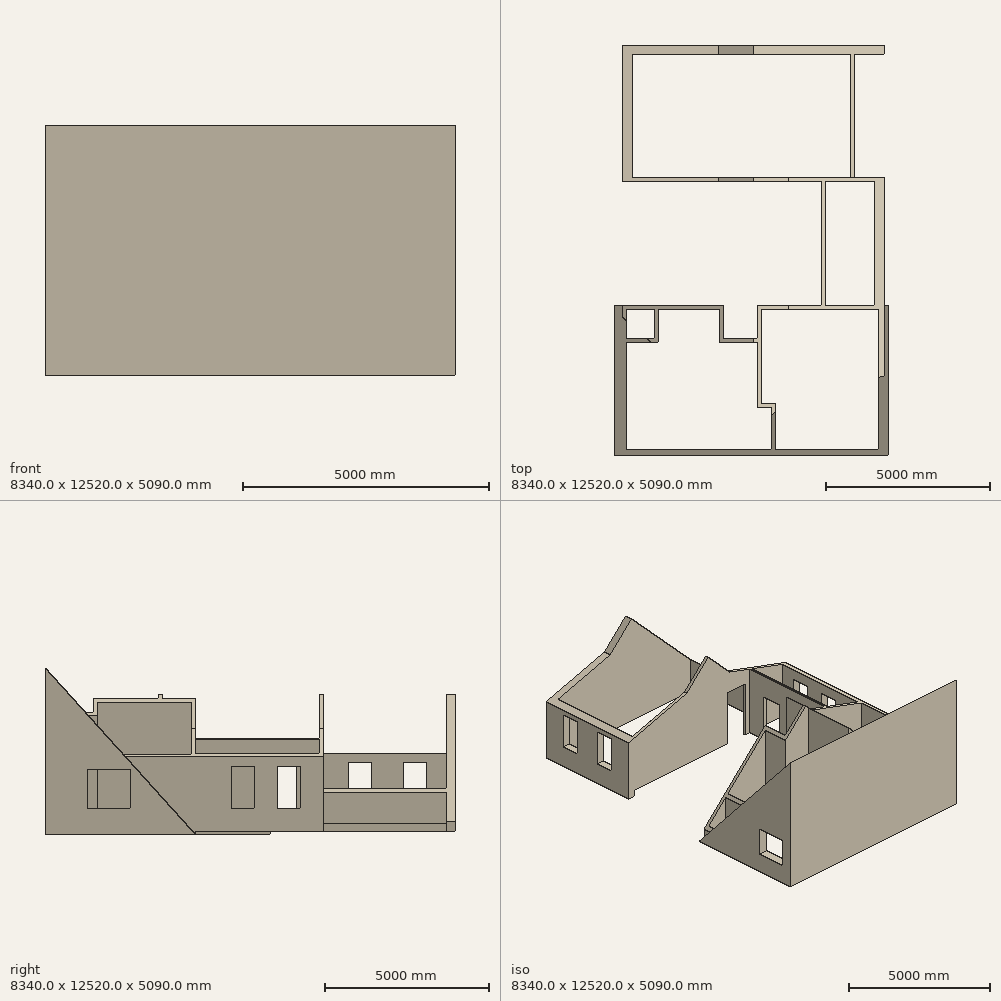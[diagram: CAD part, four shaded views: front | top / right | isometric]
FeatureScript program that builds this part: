
annotation { "Feature Type Name" : "Feature", "Feature Type Description" : "" }
export const myFeature = defineFeature(function(context is Context, id is Id, definition is map)
    precondition{}
    {
        {
            var Q0;
            Q0=qCreatedBy(makeId("Right.planeOp"),FACE);
            var sketch = newSketch(context, id + "F0", { "sketchPlane" : qUnion([Q0])});
            skLineSegment(sketch, "E0", {"start": v(2296.26, -2868.99) * mm, "end": v(-2293.74, -2868.99) * mm});
            skLineSegment(sketch, "E1", {"start": v(-2293.74, -2868.99) * mm, "end": v(-2293.74, 2221.01) * mm});
            skLineSegment(sketch, "E2", {"start": v(-2293.74, 2221.01) * mm, "end": v(2296.26, -2868.99) * mm});
            skSolve(sketch);
        }
        {
            var Q0;
            Q0=makeQuery(id+"F0.imprint","IMPRINT",FACE,{"disambiguationData":[TD([[makeQuery(id+"F0.imprint","IMPRINT",EDGE,{"derivedFrom":sQuery(id+"F0.wireOp",EDGE,"E0")}),-1.0]])]});
            extrude(context, id + "F1", {"entities" : qUnion([Q0]), "depth" : 8340 * mm});
        }
        {
            var Q0;
            Q0=makeQuery(id+"F1.opExtrude","SWEPT_FACE",FACE,{"disambiguationData":[OSD([sQuery(id+"F0.wireOp",EDGE,"E1")])]});
            cPlane(context, id + "F2", {"entities" : qUnion([Q0]), "cplaneType" : CPlaneType.OFFSET, "offset" : 12520 * mm, "oppositeDirection" : true, "width" : 150 * mm, "height" : 150 * mm});
        }
        {
            var Q0;
            Q0=qCreatedBy(id+"F2.planeOp",FACE);
            var sketch = newSketch(context, id + "F3", { "sketchPlane" : qUnion([Q0])});
            skPoint(sketch, "E3.0", {"position": v(8220, -2868.99) * mm});
            skPoint(sketch, "E4.0", {"position": v(0, -2868.99) * mm});
            skLineSegment(sketch, "E5", {"start": v(8220, -2868.99) * mm, "end": v(230, -2868.99) * mm});
            skLineSegment(sketch, "E6", {"start": v(8220, -2868.99) * mm, "end": v(8220, -2468.99) * mm});
            skLineSegment(sketch, "E7", {"start": v(8220, -2468.99) * mm, "end": v(4225, 1421.01) * mm});
            skLineSegment(sketch, "E8", {"start": v(230, -2868.99) * mm, "end": v(230, -2468.99) * mm});
            skLineSegment(sketch, "E9", {"start": v(230, -2468.99) * mm, "end": v(4225, 1421.01) * mm});
            skSolve(sketch);
        }
        {
            var Q0;
            Q0=makeQuery(id+"F3.imprint","IMPRINT",FACE,{"disambiguationData":[TD([[makeQuery(id+"F3.imprint","IMPRINT",EDGE,{"derivedFrom":sQuery(id+"F3.wireOp",EDGE,"E5")}),-1.0]])]});
            extrude(context, id + "F4", {"entities" : qUnion([Q0]), "operationType" : NewBodyOperationType.ADD, "endBound" : BoundingType.UP_TO_NEXT, "depth" : 25 * mm});
        }
        {
            var Q0;
            Q0=makeQuery(id+"F4.opExtrude","CAP_FACE",FACE,{"disambiguationData":[OSD([sQuery(id+"F3.wireOp",EDGE,"E5"),sQuery(id+"F3.wireOp",EDGE,"wZPg0SDw-hQ3W-XM3Z-Tp2p-s9tjZs1w4FBg"),sQuery(id+"F3.wireOp",EDGE,"RhiNAI7Q-V7pc-C4zH-MZjU-NtJVtZchHZu0")])],"isStart":true});
            var sketch = newSketch(context, id + "F5", { "sketchPlane" : qUnion([Q0])});
            skLineSegment(sketch, "E10", {"start": v(-230, -2868.99) * mm, "end": v(-230, -468.99) * mm});
            skLineSegment(sketch, "E11", {"start": v(-230, -468.99) * mm, "end": v(-3150.31, 374.57) * mm});
            skLineSegment(sketch, "E12", {"start": v(-3150.31, 374.57) * mm, "end": v(-230, -2868.99) * mm});
            skSolve(sketch);
        }
        {
            var Q0;
            Q0=makeQuery(id+"F5.imprint","IMPRINT",FACE,{"disambiguationData":[TD([[makeQuery(id+"F5.imprint","IMPRINT",EDGE,{"derivedFrom":sQuery(id+"F5.wireOp",EDGE,"E10")}),1.0]])]});
            extrude(context, id + "F6", {"entities" : qUnion([Q0]), "operationType" : NewBodyOperationType.ADD, "oppositeDirection" : true, "depth" : 4150 * mm});
        }
        {
            var Q0;
            Q0=makeQuery(id+"F1.opExtrude","SWEPT_FACE",FACE,{"disambiguationData":[OSD([sQuery(id+"F0.wireOp",EDGE,"E1")])]});
            cPlane(context, id + "F7", {"entities" : qUnion([Q0]), "cplaneType" : CPlaneType.OFFSET, "offset" : 8490 * mm, "oppositeDirection" : true, "width" : 150 * mm, "height" : 150 * mm});
        }
        {
            var Q0;
            Q0=qCreatedBy(id+"F7.planeOp",FACE);
            var sketch = newSketch(context, id + "F8", { "sketchPlane" : qUnion([Q0])});
            skPoint(sketch, "E13.0", {"position": v(8220, -2868.99) * mm});
            skLineSegment(sketch, "E14", {"start": v(8220, -2868.99) * mm, "end": v(8220, -468.99) * mm});
            skLineSegment(sketch, "E15", {"start": v(8220, -468.99) * mm, "end": v(5299.69, 374.57) * mm});
            skLineSegment(sketch, "E16", {"start": v(5299.69, 374.57) * mm, "end": v(8220, -2868.99) * mm});
            skPoint(sketch, "E17.0", {"position": v(3150.31, 374.57) * mm});
            skSolve(sketch);
        }
        {
            var Q0;
            {var subQ0=sQuery(id+"F8.wireOp",EDGE,"E14");Q0=makeQuery(id+"F8.imprint","IMPRINT",FACE,{"disambiguationData":[TD([[makeQuery(id+"F8.imprint","IMPRINT",EDGE,{"derivedFrom":subQ0}),1.0]])]});}
            extrude(context, id + "F9", {"entities" : qUnion([Q0]), "operationType" : NewBodyOperationType.ADD, "depth" : 8000 * mm});
        }
        {
            var Q0;
            Q0=makeQuery(id+"F4.boolean.opBoolean","MERGE",FACE,{"derivedFrom":[makeQuery(id+"F1.opExtrude","SWEPT_FACE",FACE,{"disambiguationData":[OSD([sQuery(id+"F0.wireOp",EDGE,"E0")])]}),makeQuery(id+"F4.opExtrude","SWEPT_FACE",FACE,{"disambiguationData":[OSD([sQuery(id+"F3.wireOp",EDGE,"E5")])]})]});
            cPlane(context, id + "F10", {"entities" : qUnion([Q0]), "cplaneType" : CPlaneType.OFFSET, "offset" : 6000 * mm, "oppositeDirection" : true, "width" : 150 * mm, "height" : 150 * mm});
        }
        {
            var Q0;
            Q0=qCreatedBy(id+"F10.planeOp",FACE);
            var sketch = newSketch(context, id + "F11", { "sketchPlane" : qUnion([Q0])});
            skLineSegment(sketch, "E18.0", {"start": v(230, -10226.26) * mm, "end": v(3150.31, -10226.26) * mm});
            skLineSegment(sketch, "E19.0", {"start": v(3150.31, -10226.26) * mm, "end": v(8220, -10226.26) * mm});
            skLineSegment(sketch, "E20", {"start": v(360, -1154.29) * mm, "end": v(360, 2113.74) * mm});
            skLineSegment(sketch, "E21", {"start": v(360, 2113.74) * mm, "end": v(4780, 2113.74) * mm});
            skLineSegment(sketch, "E22", {"start": v(4780, 2113.74) * mm, "end": v(4780, 833.74) * mm});
            skLineSegment(sketch, "E23", {"start": v(4780, 833.74) * mm, "end": v(4360, 833.74) * mm});
            skLineSegment(sketch, "E24", {"start": v(4360, 833.74) * mm, "end": v(4360, -1165.91) * mm});
            skLineSegment(sketch, "E25", {"start": v(4480, -2176.26) * mm, "end": v(4480, 713.74) * mm});
            skLineSegment(sketch, "E26", {"start": v(4480, 713.74) * mm, "end": v(4900, 713.74) * mm});
            skLineSegment(sketch, "E27", {"start": v(4900, 713.74) * mm, "end": v(4900, 2113.74) * mm});
            skLineSegment(sketch, "E28", {"start": v(4900, 2113.74) * mm, "end": v(8040, 2113.74) * mm});
            skLineSegment(sketch, "E29", {"start": v(8040, 2113.74) * mm, "end": v(8040, -2176.26) * mm});
            skLineSegment(sketch, "E30", {"start": v(8040, -2176.26) * mm, "end": v(4480, -2176.26) * mm});
            skLineSegment(sketch, "E31", {"start": v(530, -9936.26) * mm, "end": v(530, -6196.26) * mm});
            skLineSegment(sketch, "E32", {"start": v(7183.26, -6196.26) * mm, "end": v(7183.26, -9936.26) * mm});
            skLineSegment(sketch, "E33", {"start": v(7183.26, -9936.26) * mm, "end": v(530, -9936.26) * mm});
            skLineSegment(sketch, "E34", {"start": v(6430, -6076.26) * mm, "end": v(6430, -2296.26) * mm});
            skLineSegment(sketch, "E35", {"start": v(6430, -2296.26) * mm, "end": v(7930, -2296.26) * mm});
            skLineSegment(sketch, "E36", {"start": v(7930, -2296.26) * mm, "end": v(7930, -6076.26) * mm});
            skLineSegment(sketch, "E37", {"start": v(7930, -6076.26) * mm, "end": v(6430, -6076.26) * mm});
            skLineSegment(sketch, "E38", {"start": v(7183.26, -6196.26) * mm, "end": v(6310, -6196.26) * mm});
            skLineSegment(sketch, "E39", {"start": v(6310, -6196.26) * mm, "end": v(6310, -6196.26) * mm});
            skLineSegment(sketch, "E40", {"start": v(6310, -6196.26) * mm, "end": v(530, -6196.26) * mm});
            skLineSegment(sketch, "E41", {"start": v(6310, -2296.26) * mm, "end": v(6310, -6076.26) * mm});
            skLineSegment(sketch, "E42", {"start": v(-2.05, -2296.26) * mm, "end": v(-2.05, -6076.26) * mm});
            skLineSegment(sketch, "E43", {"start": v(360, -1154.29) * mm, "end": v(1319.1, -1154.29) * mm});
            skLineSegment(sketch, "E44", {"start": v(1319.1, -1154.29) * mm, "end": v(1319.1, -2176.26) * mm});
            skLineSegment(sketch, "E45", {"start": v(1199.1, -1274.29) * mm, "end": v(360, -1274.29) * mm});
            skLineSegment(sketch, "E46", {"start": v(360, -1274.29) * mm, "end": v(360, -2176.26) * mm});
            skLineSegment(sketch, "E47", {"start": v(360, -2176.26) * mm, "end": v(1199.1, -2176.26) * mm});
            skLineSegment(sketch, "E48", {"start": v(1199.1, -2176.26) * mm, "end": v(1199.1, -1274.29) * mm});
            skLineSegment(sketch, "E49", {"start": v(-2.05, -6076.26) * mm, "end": v(4755, -6076.26) * mm});
            skLineSegment(sketch, "E50", {"start": v(6310, -6076.26) * mm, "end": v(4755, -6076.26) * mm});
            skLineSegment(sketch, "E51", {"start": v(4755, -6076.26) * mm, "end": v(4755, -6076.26) * mm});
            skLineSegment(sketch, "E52.bottom", {"start": v(7303.26, -9936.26) * mm, "end": v(6644.3, -9936.26) * mm});
            skLineSegment(sketch, "E52.top", {"start": v(7303.26, -6196.26) * mm, "end": v(6878.23, -6196.26) * mm});
            skLineSegment(sketch, "E52.right", {"start": v(7303.26, -9936.26) * mm, "end": v(7303.26, -6196.26) * mm});
            skLineSegment(sketch, "E53", {"start": v(4360, -1165.91) * mm, "end": v(3200, -1165.91) * mm});
            skLineSegment(sketch, "E54", {"start": v(3200, -1165.91) * mm, "end": v(3200, -2176.26) * mm});
            skLineSegment(sketch, "E55", {"start": v(3200, -2176.26) * mm, "end": v(1319.1, -2176.26) * mm});
            skLineSegment(sketch, "E56", {"start": v(-2.05, -2296.26) * mm, "end": v(3320, -2296.26) * mm});
            skLineSegment(sketch, "E57", {"start": v(3320, -2296.26) * mm, "end": v(3320, -1285.91) * mm});
            skLineSegment(sketch, "E58", {"start": v(3320, -1285.91) * mm, "end": v(4360, -1285.91) * mm});
            skLineSegment(sketch, "E59", {"start": v(4360, -1285.91) * mm, "end": v(4360, -2296.26) * mm});
            skLineSegment(sketch, "E60", {"start": v(4360, -2296.26) * mm, "end": v(6310, -2296.26) * mm});
            skPoint(sketch, "E61.0", {"position": v(8220, -10226.26) * mm});
            skPoint(sketch, "E62.0", {"position": v(0, 2293.74) * mm});
            skPoint(sketch, "E63.0", {"position": v(8340, 2293.74) * mm});
            skLineSegment(sketch, "E64", {"start": v(-2.05, -2296.26) * mm, "end": v(0, 2293.74) * mm});
            skLineSegment(sketch, "E65", {"start": v(0, 2293.74) * mm, "end": v(8340, 2293.74) * mm});
            skLineSegment(sketch, "E66.bottom", {"start": v(7303.26, -9936.26) * mm, "end": v(8220, -9936.26) * mm});
            skLineSegment(sketch, "E66.left", {"start": v(7303.26, -9936.26) * mm, "end": v(7303.26, -7396.26) * mm});
            skLineSegment(sketch, "E66.right", {"start": v(8220, -9936.26) * mm, "end": v(8220, -6196.26) * mm});
            skLineSegment(sketch, "E67.0.0", {"start": v(5299.69, 628.68) * mm, "end": v(5299.69, 628.68) * mm});
            skLineSegment(sketch, "E67.0.1", {"start": v(8220, -2296.26) * mm, "end": v(8220, -6196.26) * mm});
            skLineSegment(sketch, "E68", {"start": v(7303.26, -6196.26) * mm, "end": v(8220, -6196.26) * mm});
            skPoint(sketch, "E69.0", {"position": v(8220, -2296.26) * mm});
            skLineSegment(sketch, "E70", {"start": v(8220, -2296.26) * mm, "end": v(8340, -2296.26) * mm});
            skPoint(sketch, "E71.0", {"position": v(8340, -2296.26) * mm});
            skLineSegment(sketch, "E72", {"start": v(8340, -2296.26) * mm, "end": v(8340, 2293.74) * mm});
            skSolve(sketch);
        }
        {
            var Q0;
            Q0=makeQuery(id+"F11.imprint","IMPRINT",FACE,{"disambiguationData":[TD([[makeQuery(id+"F11.imprint","IMPRINT",EDGE,{"derivedFrom":sQuery(id+"F11.wireOp",EDGE,"E25")}),-1.0]])]});
            var Q1;
            Q1=makeQuery(id+"F11.imprint","IMPRINT",FACE,{"disambiguationData":[TD([[makeQuery(id+"F11.imprint","IMPRINT",EDGE,{"derivedFrom":sQuery(id+"F11.wireOp",EDGE,"E41")}),-1.0]])]});
            var Q2;
            Q2=makeQuery(id+"F11.imprint","IMPRINT",FACE,{"disambiguationData":[TD([[makeQuery(id+"F11.imprint","IMPRINT",EDGE,{"derivedFrom":sQuery(id+"F11.wireOp",EDGE,"E34")}),-1.0]])]});
            var Q3;
            Q3=makeQuery(id+"F11.imprint","IMPRINT",FACE,{"disambiguationData":[TD([[makeQuery(id+"F11.imprint","IMPRINT",EDGE,{"derivedFrom":sQuery(id+"F11.wireOp",EDGE,"E31")}),-1.0]])]});
            var Q4;
            Q4=makeQuery(id+"F11.imprint","IMPRINT",FACE,{"disambiguationData":[TD([[makeQuery(id+"F11.imprint","IMPRINT",EDGE,{"derivedFrom":sQuery(id+"F11.wireOp",EDGE,"E20")}),-1.0]])]});
            var Q5;
            Q5=makeQuery(id+"F11.imprint","IMPRINT",FACE,{"disambiguationData":[TD([[makeQuery(id+"F11.imprint","IMPRINT",EDGE,{"derivedFrom":sQuery(id+"F11.wireOp",EDGE,"E45")}),1.0]])]});
            var Q6;
            Q6=makeQuery(id+"F11.imprint","IMPRINT",FACE,{"disambiguationData":[TD([[makeQuery(id+"F11.imprint","IMPRINT",EDGE,{"derivedFrom":sQuery(id+"F11.wireOp",EDGE,"E66.bottom")}),1.0]])]});
            extrude(context, id + "F12", {"entities" : qUnion([Q0, Q1, Q2, Q3, Q4, Q5, Q6]), "operationType" : NewBodyOperationType.REMOVE, "endBound" : BoundingType.THROUGH_ALL, "depth" : 25 * mm});
        }
        {
            var Q0;
            Q0=makeQuery(id+"F12.boolean.opBoolean","COPY",FACE,{"derivedFrom":makeQuery(id+"F12.opExtrude","SWEPT_FACE",FACE,{"disambiguationData":[OSD([sQuery(id+"F11.wireOp",EDGE,"E41")])]})});
            var sketch = newSketch(context, id + "F13", { "sketchPlane" : qUnion([Q0])});
            skLineSegment(sketch, "E73.bottom", {"start": v(-5376.26, -2868.99) * mm, "end": v(-4576.26, -2868.99) * mm});
            skLineSegment(sketch, "E73.top", {"start": v(-5376.26, -768.99) * mm, "end": v(-4576.26, -768.99) * mm});
            skLineSegment(sketch, "E73.left", {"start": v(-5376.26, -2868.99) * mm, "end": v(-5376.26, -768.99) * mm});
            skLineSegment(sketch, "E73.right", {"start": v(-4576.26, -2868.99) * mm, "end": v(-4576.26, -768.99) * mm});
            skSolve(sketch);
        }
        {
            var Q0;
            Q0=makeQuery(id+"F13.imprint","IMPRINT",FACE,{"disambiguationData":[TD([[makeQuery(id+"F13.imprint","IMPRINT",EDGE,{"derivedFrom":sQuery(id+"F13.wireOp",EDGE,"E73.bottom")}),1.0]])]});
            extrude(context, id + "F14", {"entities" : qUnion([Q0]), "operationType" : NewBodyOperationType.REMOVE, "endBound" : BoundingType.UP_TO_NEXT, "oppositeDirection" : true, "depth" : 25 * mm});
        }
        {
            var Q0;
            Q0=makeQuery(id+"F6.opExtrude","SWEPT_FACE",FACE,{"disambiguationData":[OSD([sQuery(id+"F5.wireOp",EDGE,"E10")])]});
            var sketch = newSketch(context, id + "F15", { "sketchPlane" : qUnion([Q0])});
            skLineSegment(sketch, "E74.bottom", {"start": v(-9351.26, -668.99) * mm, "end": v(-8651.26, -668.99) * mm});
            skLineSegment(sketch, "E74.top", {"start": v(-9351.26, -1968.99) * mm, "end": v(-8651.26, -1968.99) * mm});
            skLineSegment(sketch, "E74.left", {"start": v(-9351.26, -668.99) * mm, "end": v(-9351.26, -1968.99) * mm});
            skLineSegment(sketch, "E74.right", {"start": v(-8651.26, -668.99) * mm, "end": v(-8651.26, -1968.99) * mm});
            skLineSegment(sketch, "E75.bottom", {"start": v(-7651.26, -668.99) * mm, "end": v(-6951.26, -668.99) * mm});
            skLineSegment(sketch, "E75.top", {"start": v(-7651.26, -1968.99) * mm, "end": v(-6951.26, -1968.99) * mm});
            skLineSegment(sketch, "E75.left", {"start": v(-7651.26, -668.99) * mm, "end": v(-7651.26, -1968.99) * mm});
            skLineSegment(sketch, "E75.right", {"start": v(-6951.26, -668.99) * mm, "end": v(-6951.26, -1968.99) * mm});
            skSolve(sketch);
        }
        {
            var Q0;
            Q0=makeQuery(id+"F15.imprint","IMPRINT",FACE,{"disambiguationData":[TD([[makeQuery(id+"F15.imprint","IMPRINT",EDGE,{"derivedFrom":sQuery(id+"F15.wireOp",EDGE,"E74.bottom")}),-1.0]])]});
            var Q1;
            Q1=makeQuery(id+"F15.imprint","IMPRINT",FACE,{"disambiguationData":[TD([[makeQuery(id+"F15.imprint","IMPRINT",EDGE,{"derivedFrom":sQuery(id+"F15.wireOp",EDGE,"E75.bottom")}),-1.0]])]});
            extrude(context, id + "F16", {"entities" : qUnion([Q0, Q1]), "operationType" : NewBodyOperationType.REMOVE, "endBound" : BoundingType.UP_TO_NEXT, "oppositeDirection" : true, "depth" : 25 * mm});
        }
        {
            var Q0;
            Q0=makeQuery(id+"F1.opExtrude","CAP_FACE",FACE,{"disambiguationData":[OSD([sQuery(id+"F0.wireOp",EDGE,"E0"),sQuery(id+"F0.wireOp",EDGE,"E1"),sQuery(id+"F0.wireOp",EDGE,"E2")])],"isStart":true});
            var sketch = newSketch(context, id + "F17", { "sketchPlane" : qUnion([Q0])});
            skLineSegment(sketch, "E76.bottom", {"start": v(733.74, -1138.99) * mm, "end": v(1863.74, -1138.99) * mm});
            skLineSegment(sketch, "E76.top", {"start": v(733.74, -2168.99) * mm, "end": v(1863.74, -2168.99) * mm});
            skLineSegment(sketch, "E76.left", {"start": v(733.74, -1138.99) * mm, "end": v(733.74, -2168.99) * mm});
            skLineSegment(sketch, "E76.right", {"start": v(1863.74, -1138.99) * mm, "end": v(1863.74, -2168.99) * mm});
            skSolve(sketch);
        }
        {
            var Q0;
            Q0=makeQuery(id+"F17.imprint","IMPRINT",FACE,{"disambiguationData":[TD([[makeQuery(id+"F17.imprint","IMPRINT",EDGE,{"derivedFrom":sQuery(id+"F17.wireOp",EDGE,"E76.bottom")}),-1.0]])]});
            extrude(context, id + "F18", {"entities" : qUnion([Q0]), "operationType" : NewBodyOperationType.REMOVE, "endBound" : BoundingType.UP_TO_NEXT, "oppositeDirection" : true, "depth" : 25 * mm});
        }
        {
            var Q0;
            Q0=makeQuery(id+"F9.boolean.opBoolean","MERGE",FACE,{"derivedFrom":[makeQuery(id+"F1.opExtrude","CAP_FACE",FACE,{"disambiguationData":[OSD([sQuery(id+"F0.wireOp",EDGE,"E0"),sQuery(id+"F0.wireOp",EDGE,"E1"),sQuery(id+"F0.wireOp",EDGE,"E2")])],"isStart":false}),makeQuery(id+"F9.opExtrude","SWEPT_FACE",FACE,{"disambiguationData":[OSD([sQuery(id+"F8.wireOp",EDGE,"E14")])]})]});
            var sketch = newSketch(context, id + "F19", { "sketchPlane" : qUnion([Q0])});
            skLineSegment(sketch, "E77.bottom", {"start": v(306.26, -2068.99) * mm, "end": v(-1013.74, -2068.99) * mm});
            skLineSegment(sketch, "E77.top", {"start": v(306.26, -868.99) * mm, "end": v(-1013.74, -868.99) * mm});
            skLineSegment(sketch, "E77.left", {"start": v(-1013.74, -868.99) * mm, "end": v(-1013.74, -2068.99) * mm});
            skLineSegment(sketch, "E77.right", {"start": v(306.26, -868.99) * mm, "end": v(306.26, -2068.99) * mm});
            skLineSegment(sketch, "E78.bottom", {"start": v(4096.26, -2068.99) * mm, "end": v(3396.26, -2068.99) * mm});
            skLineSegment(sketch, "E78.top", {"start": v(4096.26, -768.99) * mm, "end": v(3396.26, -768.99) * mm});
            skLineSegment(sketch, "E78.left", {"start": v(3396.26, -768.99) * mm, "end": v(3396.26, -2068.99) * mm});
            skLineSegment(sketch, "E78.right", {"start": v(4096.26, -768.99) * mm, "end": v(4096.26, -2068.99) * mm});
            skLineSegment(sketch, "E79.bottom", {"start": v(4796.26, -768.99) * mm, "end": v(5496.26, -768.99) * mm});
            skLineSegment(sketch, "E79.top", {"start": v(4796.26, -2068.99) * mm, "end": v(5496.26, -2068.99) * mm});
            skLineSegment(sketch, "E79.left", {"start": v(4796.26, -768.99) * mm, "end": v(4796.26, -2068.99) * mm});
            skLineSegment(sketch, "E79.right", {"start": v(5496.26, -768.99) * mm, "end": v(5496.26, -2068.99) * mm});
            skSolve(sketch);
        }
        {
            var Q0;
            Q0=makeQuery(id+"F19.imprint","IMPRINT",FACE,{"disambiguationData":[TD([[makeQuery(id+"F19.imprint","IMPRINT",EDGE,{"derivedFrom":sQuery(id+"F19.wireOp",EDGE,"E77.bottom")}),-1.0]])]});
            var Q1;
            Q1=makeQuery(id+"F19.imprint","IMPRINT",FACE,{"disambiguationData":[TD([[makeQuery(id+"F19.imprint","IMPRINT",EDGE,{"derivedFrom":sQuery(id+"F19.wireOp",EDGE,"E78.bottom")}),-1.0]])]});
            var Q2;
            Q2=makeQuery(id+"F19.imprint","IMPRINT",FACE,{"disambiguationData":[TD([[makeQuery(id+"F19.imprint","IMPRINT",EDGE,{"derivedFrom":sQuery(id+"F19.wireOp",EDGE,"E79.bottom")}),-1.0]])]});
            extrude(context, id + "F20", {"entities" : qUnion([Q0, Q1, Q2]), "operationType" : NewBodyOperationType.REMOVE, "endBound" : BoundingType.SYMMETRIC, "oppositeDirection" : true, "depth" : 600 * mm});
        }
        {
            var Q0;
            Q0=makeQuery(id+"F12.boolean.opBoolean","COPY",FACE,{"derivedFrom":makeQuery(id+"F12.opExtrude","SWEPT_FACE",FACE,{"disambiguationData":[OSD([sQuery(id+"F11.wireOp",EDGE,"E58")])]})});
            var sketch = newSketch(context, id + "F21", { "sketchPlane" : qUnion([Q0])});
            skLineSegment(sketch, "E80.bottom", {"start": v(-4199.89, -2868.99) * mm, "end": v(-3499.89, -2868.99) * mm});
            skLineSegment(sketch, "E80.top", {"start": v(-4199.89, -768.99) * mm, "end": v(-3499.89, -768.99) * mm});
            skLineSegment(sketch, "E80.left", {"start": v(-4199.89, -2868.99) * mm, "end": v(-4199.89, -768.99) * mm});
            skLineSegment(sketch, "E80.right", {"start": v(-3499.89, -2868.99) * mm, "end": v(-3499.89, -768.99) * mm});
            skSolve(sketch);
        }
        {
            var Q0;
            Q0=makeQuery(id+"F21.imprint","IMPRINT",FACE,{"disambiguationData":[TD([[makeQuery(id+"F21.imprint","IMPRINT",EDGE,{"derivedFrom":sQuery(id+"F21.wireOp",EDGE,"E80.bottom")}),1.0]])]});
            extrude(context, id + "F22", {"entities" : qUnion([Q0]), "operationType" : NewBodyOperationType.REMOVE, "endBound" : BoundingType.UP_TO_NEXT, "oppositeDirection" : true, "depth" : 25 * mm});
        }
        {
            var Q0;
            Q0=makeQuery(id+"F12.boolean.opBoolean","COPY",FACE,{"derivedFrom":makeQuery(id+"F12.opExtrude","SWEPT_FACE",FACE,{"disambiguationData":[OSD([sQuery(id+"F11.wireOp",EDGE,"E59")])]})});
            var sketch = newSketch(context, id + "F23", { "sketchPlane" : qUnion([Q0])});
            skLineSegment(sketch, "E81.bottom", {"start": v(-2146.26, -2868.99) * mm, "end": v(-1346.26, -2868.99) * mm});
            skLineSegment(sketch, "E81.top", {"start": v(-2146.26, -768.99) * mm, "end": v(-1346.26, -768.99) * mm});
            skLineSegment(sketch, "E81.left", {"start": v(-2146.26, -2868.99) * mm, "end": v(-2146.26, -768.99) * mm});
            skLineSegment(sketch, "E81.right", {"start": v(-1346.26, -2868.99) * mm, "end": v(-1346.26, -768.99) * mm});
            skSolve(sketch);
        }
        {
            var Q0;
            Q0=makeQuery(id+"F23.imprint","IMPRINT",FACE,{"disambiguationData":[TD([[makeQuery(id+"F23.imprint","IMPRINT",EDGE,{"derivedFrom":sQuery(id+"F23.wireOp",EDGE,"E81.bottom")}),1.0]])]});
            extrude(context, id + "F24", {"entities" : qUnion([Q0]), "operationType" : NewBodyOperationType.REMOVE, "endBound" : BoundingType.UP_TO_NEXT, "oppositeDirection" : true, "depth" : 25 * mm});
        }
        {
            var Q0;
            Q0=makeQuery(id+"F4.boolean.opBoolean","MERGE",FACE,{"derivedFrom":[makeQuery(id+"F1.opExtrude","SWEPT_FACE",FACE,{"disambiguationData":[OSD([sQuery(id+"F0.wireOp",EDGE,"E0")])]}),makeQuery(id+"F4.opExtrude","SWEPT_FACE",FACE,{"disambiguationData":[OSD([sQuery(id+"F3.wireOp",EDGE,"E5")])]})]});
            var sketch = newSketch(context, id + "F25", { "sketchPlane" : qUnion([Q0])});
            skLineSegment(sketch, "E82.bottom", {"start": v(8340, -2296.26) * mm, "end": v(230, -2296.26) * mm});
            skLineSegment(sketch, "E82.top", {"start": v(8340, -10226.26) * mm, "end": v(230, -10226.26) * mm});
            skLineSegment(sketch, "E82.left", {"start": v(8340, -2296.26) * mm, "end": v(8340, -10226.26) * mm});
            skLineSegment(sketch, "E82.right", {"start": v(230, -2296.26) * mm, "end": v(230, -10226.26) * mm});
            skSolve(sketch);
        }
        {
            var Q0;
            {var subQ1=sQuery(id+"F3.wireOp",EDGE,"E5");var subQ2=makeQuery(id+"F4.opExtrude","SWEPT_FACE",FACE,{"disambiguationData":[OSD([subQ1])]});var subQ3=sQuery(id+"F0.wireOp",EDGE,"E0");var subQ4=makeQuery(id+"F1.opExtrude","SWEPT_FACE",FACE,{"disambiguationData":[OSD([subQ3])]});var subQ5=makeQuery(id+"F4.boolean.opBoolean","MERGE",FACE,{"derivedFrom":[subQ4,subQ2]});Q0=makeQuery(id+"F25.imprint","IMPRINT",FACE,{"disambiguationData":[TD([[makeQuery(id+"F25.imprint","IMPRINT",EDGE,{"derivedFrom":makeQuery(id+"F12.boolean.opBoolean","INTERSECT",EDGE,{"derivedFrom":[subQ5,makeQuery(id+"F12.opExtrude","SWEPT_FACE",FACE,{"disambiguationData":[OSD([sQuery(id+"F11.wireOp",EDGE,"E31")])]})]})}),-1.0]])]});}
            var Q1;
            {var subQ1=sQuery(id+"F13.wireOp",EDGE,"E73.right");var subQ4=sQuery(id+"F3.wireOp",EDGE,"E5");var subQ6=sQuery(id+"F0.wireOp",EDGE,"E0");var subQ10=sQuery(id+"F11.wireOp",EDGE,"E41");Q1=makeQuery(id+"F25.imprint","IMPRINT",FACE,{"disambiguationData":[TD([[makeQuery(id+"F25.imprint","IMPRINT",EDGE,{"derivedFrom":makeQuery(id+"F14.boolean.opBoolean","COPY",EDGE,{"derivedFrom":makeQuery(id+"F14.opExtrude","SWEPT_EDGE",EDGE,{"disambiguationData":[OSD([subQ6,subQ4,subQ10,sQuery(id+"F13.wireOp",EDGE,"E73.bottom"),subQ1])]})})}),-1.0]])]});}
            extrude(context, id + "F26", {"entities" : qUnion([Q0, Q1]), "operationType" : NewBodyOperationType.REMOVE, "oppositeDirection" : true, "depth" : 100 * mm});
        }
        {
            var Q0;
            Q0=makeQuery(id+"F26.boolean.opBoolean","COPY",FACE,{"derivedFrom":makeQuery(id+"F26.opExtrude","CAP_FACE",FACE,{"disambiguationData":[OSD([sQuery(id+"F0.wireOp",EDGE,"E0"),sQuery(id+"F3.wireOp",EDGE,"E5"),sQuery(id+"F3.wireOp",EDGE,"E6"),sQuery(id+"F11.wireOp",EDGE,"E31"),sQuery(id+"F11.wireOp",EDGE,"E32"),sQuery(id+"F11.wireOp",EDGE,"E33"),sQuery(id+"F11.wireOp",EDGE,"E34"),sQuery(id+"F11.wireOp",EDGE,"E36"),sQuery(id+"F11.wireOp",EDGE,"E37"),sQuery(id+"F11.wireOp",EDGE,"E38"),sQuery(id+"F11.wireOp",EDGE,"E40"),sQuery(id+"F11.wireOp",EDGE,"E41"),sQuery(id+"F11.wireOp",EDGE,"E49"),sQuery(id+"F11.wireOp",EDGE,"E50"),sQuery(id+"F11.wireOp",EDGE,"E52.bottom"),sQuery(id+"F11.wireOp",EDGE,"E52.top"),sQuery(id+"F11.wireOp",EDGE,"E52.right"),sQuery(id+"F11.wireOp",EDGE,"E66.bottom"),sQuery(id+"F11.wireOp",EDGE,"E66.left"),sQuery(id+"F11.wireOp",EDGE,"E68"),sQuery(id+"F13.wireOp",EDGE,"E73.bottom"),sQuery(id+"F13.wireOp",EDGE,"E73.left"),sQuery(id+"F25.wireOp",EDGE,"E82.bottom"),sQuery(id+"F25.wireOp",EDGE,"E82.top"),sQuery(id+"F25.wireOp",EDGE,"E82.right")])],"isStart":false})});
            var sketch = newSketch(context, id + "F27", { "sketchPlane" : qUnion([Q0])});
            skPoint(sketch, "E83.0", {"position": v(530, -6196.26) * mm});
            skPoint(sketch, "E84.0", {"position": v(7183.26, -9936.26) * mm});
            skPoint(sketch, "E85.0", {"position": v(7303.26, -9936.26) * mm});
            skPoint(sketch, "E86.0", {"position": v(7930, -6076.26) * mm});
            skPoint(sketch, "E87.0", {"position": v(6430, -2296.26) * mm});
            skPoint(sketch, "E88.0", {"position": v(6310, -2296.26) * mm});
            skPoint(sketch, "E89.0", {"position": v(6310, -6076.26) * mm});
            skPoint(sketch, "E90.0", {"position": v(6430, -6076.26) * mm});
            skLineSegment(sketch, "E91", {"start": v(6430, -2296.26) * mm, "end": v(6310, -2296.26) * mm});
            skLineSegment(sketch, "E92", {"start": v(6310, -2296.26) * mm, "end": v(6310, -6076.26) * mm});
            skLineSegment(sketch, "E93", {"start": v(6310, -6076.26) * mm, "end": v(530, -6076.26) * mm});
            skLineSegment(sketch, "E94", {"start": v(530, -6076.26) * mm, "end": v(530, -6196.26) * mm});
            skPoint(sketch, "E95.0", {"position": v(7183.26, -6196.26) * mm});
            skPoint(sketch, "E96.0", {"position": v(7303.26, -6196.26) * mm});
            skLineSegment(sketch, "E97", {"start": v(530, -6196.26) * mm, "end": v(7183.26, -6196.26) * mm});
            skLineSegment(sketch, "E98", {"start": v(7183.26, -9936.26) * mm, "end": v(7183.26, -6196.26) * mm});
            skLineSegment(sketch, "E99", {"start": v(7183.26, -9936.26) * mm, "end": v(7303.26, -9936.26) * mm});
            skLineSegment(sketch, "E100", {"start": v(7303.26, -9936.26) * mm, "end": v(7303.26, -6196.26) * mm});
            skLineSegment(sketch, "E101", {"start": v(7930, -6196.26) * mm, "end": v(7930, -6076.26) * mm});
            skLineSegment(sketch, "E102", {"start": v(7930, -6076.26) * mm, "end": v(6430, -6076.26) * mm});
            skLineSegment(sketch, "E103", {"start": v(6430, -6076.26) * mm, "end": v(6430, -2296.26) * mm});
            skSolve(sketch);
        }
        {
            var Q0;
            {var subQ7=sQuery(id+"F27.wireOp",EDGE,"E93");Q0=makeQuery(id+"F27.imprint","IMPRINT",FACE,{"disambiguationData":[TD([[makeQuery(id+"F27.imprint","IMPRINT",EDGE,{"derivedFrom":subQ7}),1.0]])]});}
            var Q1;
            {var subQ0=sQuery(id+"F27.wireOp",EDGE,"E91");Q1=makeQuery(id+"F27.imprint","IMPRINT",FACE,{"disambiguationData":[TD([[makeQuery(id+"F27.imprint","IMPRINT",EDGE,{"derivedFrom":subQ0}),1.0]])]});}
            extrude(context, id + "F28", {"entities" : qUnion([Q0, Q1]), "operationType" : NewBodyOperationType.REMOVE, "oppositeDirection" : true, "depth" : 240 * mm});
        }
        {
            var Q0;
            Q0=makeQuery(id+"F12.boolean.opBoolean","MERGE",FACE,{"derivedFrom":[makeQuery(id+"F6.opExtrude","CAP_FACE",FACE,{"disambiguationData":[OSD([sQuery(id+"F5.wireOp",EDGE,"E10"),sQuery(id+"F5.wireOp",EDGE,"E11"),sQuery(id+"F5.wireOp",EDGE,"E12")])],"isStart":false}),makeQuery(id+"F12.opExtrude","SWEPT_FACE",FACE,{"disambiguationData":[OSD([sQuery(id+"F11.wireOp",EDGE,"E49"),sQuery(id+"F11.wireOp",EDGE,"E50")])]})]});
            var sketch = newSketch(context, id + "F29", { "sketchPlane" : qUnion([Q0])});
            skLineSegment(sketch, "E104.bottom", {"start": v(6090.04, -2528.99) * mm, "end": v(5190.04, -2528.99) * mm});
            skLineSegment(sketch, "E104.top", {"start": v(6090.04, -428.99) * mm, "end": v(5190.04, -428.99) * mm});
            skLineSegment(sketch, "E104.left", {"start": v(6090.04, -2528.99) * mm, "end": v(6090.04, -428.99) * mm});
            skLineSegment(sketch, "E104.right", {"start": v(5190.04, -2528.99) * mm, "end": v(5190.04, -428.99) * mm});
            skSolve(sketch);
        }
        {
            var Q0;
            Q0=makeQuery(id+"F29.imprint","IMPRINT",FACE,{"disambiguationData":[TD([[makeQuery(id+"F29.imprint","IMPRINT",EDGE,{"derivedFrom":sQuery(id+"F29.wireOp",EDGE,"E104.bottom")}),-1.0]])]});
            extrude(context, id + "F30", {"entities" : qUnion([Q0]), "operationType" : NewBodyOperationType.REMOVE, "endBound" : BoundingType.UP_TO_NEXT, "oppositeDirection" : true, "depth" : 25 * mm});
        }
    });
